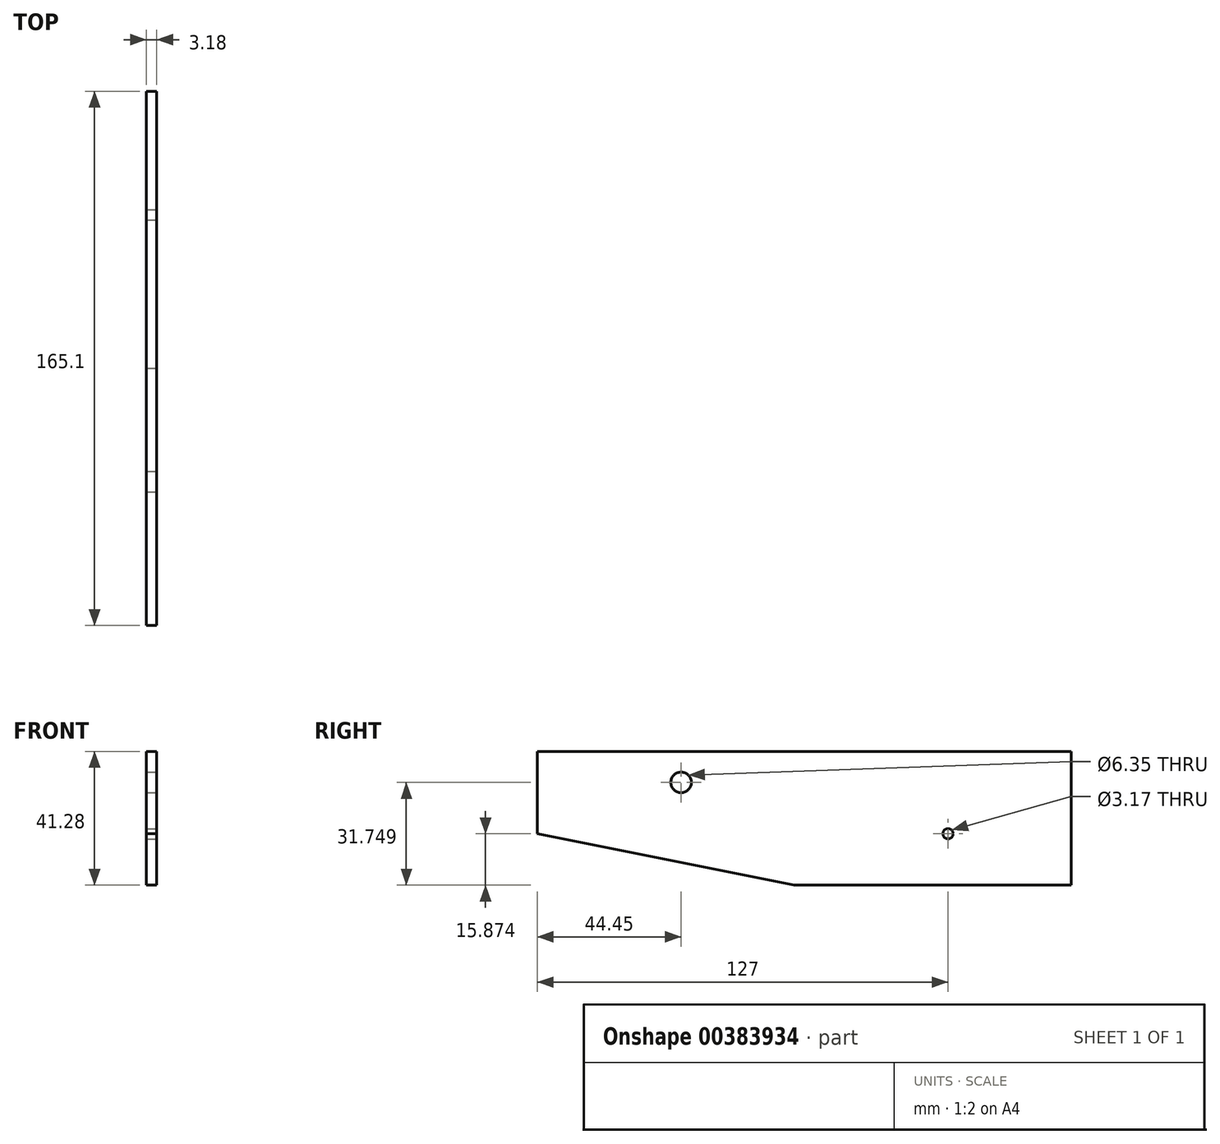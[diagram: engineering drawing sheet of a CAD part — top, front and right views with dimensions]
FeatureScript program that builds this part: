
annotation { "Feature Type Name" : "Feature", "Feature Type Description" : "" }
export const myFeature = defineFeature(function(context is Context, id is Id, definition is map)
    precondition{}
    {
        {
            var Q0;
            Q0=qCreatedBy(makeId("Right.planeOp"),FACE);
            var sketch = newSketch(context, id + "F0", { "sketchPlane" : qUnion([Q0])});
            skLineSegment(sketch, "E0.bottom", {"start": v(57.15, 46.04) * mm, "end": v(-107.95, 46.04) * mm});
            skLineSegment(sketch, "E0.left", {"start": v(57.15, 46.04) * mm, "end": v(57.15, 4.76) * mm});
            skPoint(sketch, "E0.middle", {"position": v(-25.4, 25.4) * mm});
            skLineSegment(sketch, "E1", {"start": v(57.15, 4.76) * mm, "end": v(-28.57, 4.76) * mm});
            skLineSegment(sketch, "E2", {"start": v(-107.95, 46.04) * mm, "end": v(-107.95, 20.64) * mm});
            skLineSegment(sketch, "E3", {"start": v(-107.95, 20.64) * mm, "end": v(-28.57, 4.76) * mm});
            skSolve(sketch);
        }
        {
            var Q0;
            Q0=qCreatedBy(makeId("Right.planeOp"),FACE);
            var sketch = newSketch(context, id + "F1", { "sketchPlane" : qUnion([Q0])});
            skCircle(sketch, "E4", {"center": v(19.05, 20.63) * mm, "radius": 1.59 * mm});
            skCircle(sketch, "E5", {"center": v(-63.5, 36.5) * mm, "radius": 3.18 * mm});
            skSolve(sketch);
        }
        {
            var Q0;
            Q0=qCreatedBy(makeId("Right.planeOp"),FACE);
            var sketch = newSketch(context, id + "F2", { "sketchPlane" : qUnion([Q0])});
            skCircle(sketch, "E6", {"center": v(-31.75, 30.16) * mm, "radius": 6.35 * mm});
            skSolve(sketch);
        }
        {
            var Q0;
            Q0 = qSketchRegion(id + "F0", true);
            extrude(context, id + "F3", {"entities" : qUnion([Q0]), "endBound" : BoundingType.SYMMETRIC, "depth" : 3.17 * mm});
        }
        {
            var Q0;
            Q0 = qSketchRegion(id + "F1", true);
            extrude(context, id + "F4", {"entities" : qUnion([Q0]), "operationType" : NewBodyOperationType.REMOVE, "endBound" : BoundingType.SYMMETRIC, "oppositeDirection" : true, "depth" : 25.4 * mm});
        }
    });
